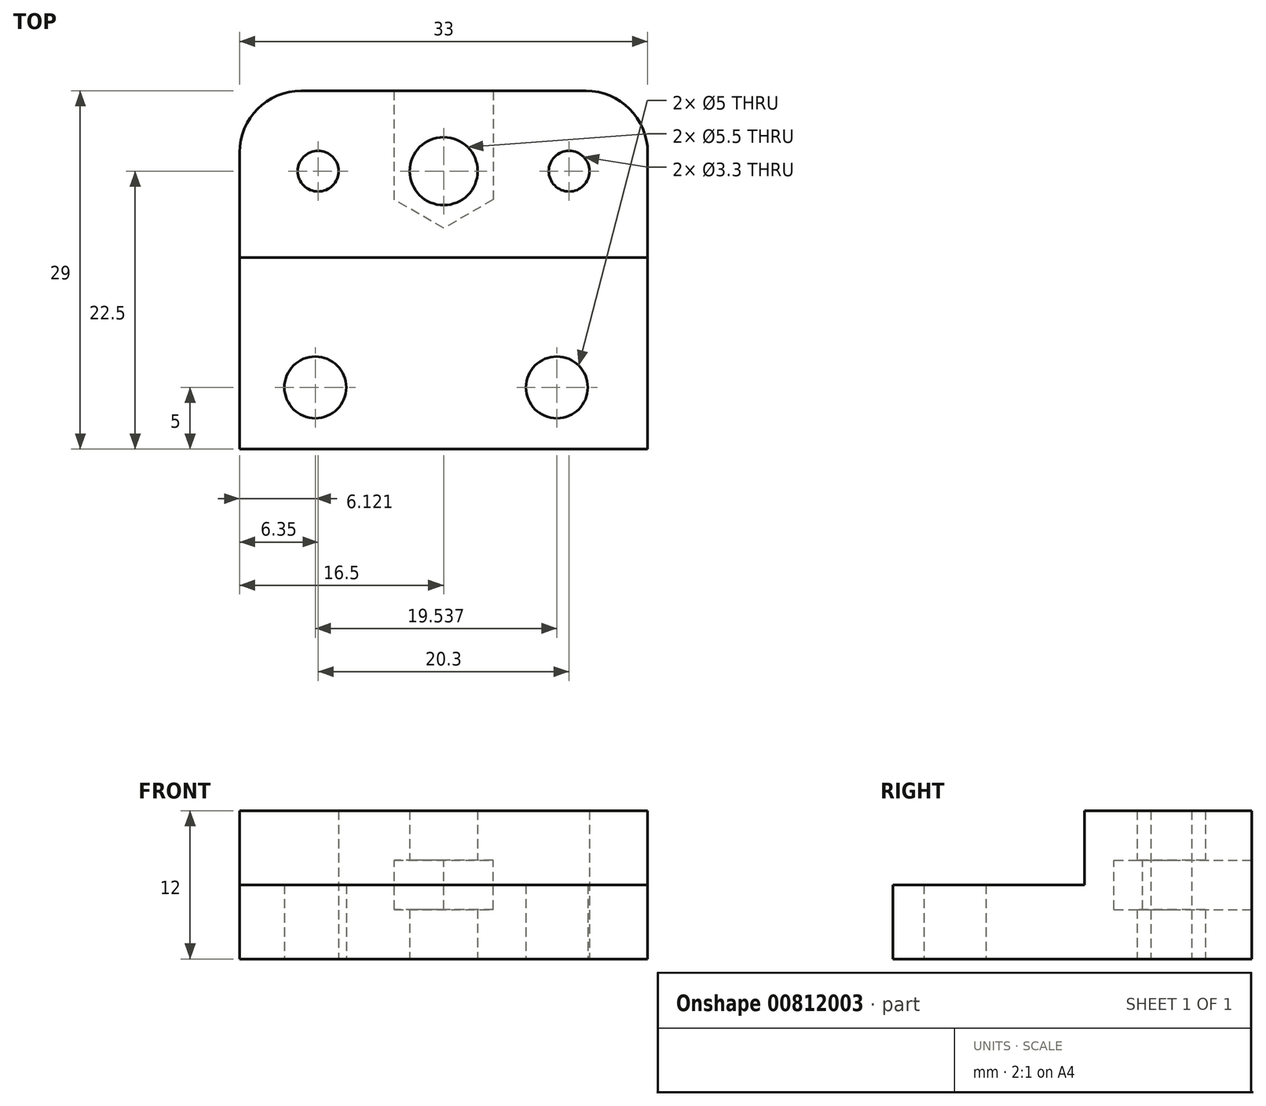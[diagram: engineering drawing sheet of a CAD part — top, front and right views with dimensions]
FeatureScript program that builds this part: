
annotation { "Feature Type Name" : "Feature", "Feature Type Description" : "" }
export const myFeature = defineFeature(function(context is Context, id is Id, definition is map)
    precondition{}
    {
        {
            var Q0;
            Q0=qCreatedBy(makeId("Top.planeOp"),FACE);
            var sketch = newSketch(context, id + "F0", { "sketchPlane" : qUnion([Q0])});
            skLineSegment(sketch, "E0.bottom", {"start": v(-16.5, 14.5) * mm, "end": v(16.5, 14.5) * mm});
            skLineSegment(sketch, "E0.top", {"start": v(-16.5, -14.5) * mm, "end": v(16.5, -14.5) * mm});
            skLineSegment(sketch, "E0.left", {"start": v(-16.5, 14.5) * mm, "end": v(-16.5, -14.5) * mm});
            skLineSegment(sketch, "E0.right", {"start": v(16.5, 14.5) * mm, "end": v(16.5, -14.5) * mm});
            skPoint(sketch, "E0.middle", {"position": v(0, 0) * mm});
            skCircle(sketch, "E1", {"center": v(0, 8) * mm, "radius": 2.75 * mm});
            skCircle(sketch, "E2", {"center": v(-10.38, -9.5) * mm, "radius": 2.5 * mm});
            skCircle(sketch, "E3", {"center": v(9.16, -9.5) * mm, "radius": 2.5 * mm});
            skLineSegment(sketch, "E4", {"start": v(-10.38, -9.5) * mm, "end": v(9.16, -9.5) * mm, "construction": true});
            skCircle(sketch, "E5", {"center": v(10.15, 8) * mm, "radius": 1.65 * mm});
            skCircle(sketch, "E6", {"center": v(-10.15, 8) * mm, "radius": 1.65 * mm});
            skCircle(sketch, "E7.cCircle", {"center": v(0, 8) * mm, "radius": 4 * mm, "construction": true});
            skLineSegment(sketch, "E7.0", {"start": v(4, 10.3) * mm, "end": v(4, 5.7) * mm});
            skLineSegment(sketch, "E7.1", {"start": v(4, 5.7) * mm, "end": v(0, 3.38) * mm});
            skLineSegment(sketch, "E7.2", {"start": v(0, 3.38) * mm, "end": v(-4, 5.7) * mm});
            skLineSegment(sketch, "E7.3", {"start": v(-4, 5.7) * mm, "end": v(-4, 10.12) * mm});
            skPoint(sketch, "E7.0.midPoint", {"position": v(4, 8) * mm});
            skPoint(sketch, "E8.orphan", {"position": v(0, 12.62) * mm});
            skLineSegment(sketch, "E9", {"start": v(-4, 10.12) * mm, "end": v(-4, 14.5) * mm});
            skLineSegment(sketch, "E10", {"start": v(4, 10.3) * mm, "end": v(4, 14.5) * mm});
            skLineSegment(sketch, "E11.top", {"start": v(-16.5, 1) * mm, "end": v(16.5, 1) * mm});
            skLineSegment(sketch, "E11.left", {"start": v(-16.5, -14.5) * mm, "end": v(-16.5, 1) * mm});
            skLineSegment(sketch, "E11.right", {"start": v(16.5, -14.5) * mm, "end": v(16.5, 1) * mm});
            skSolve(sketch);
        }
        {
            var Q0;
            Q0=makeQuery(id+"F0.imprint","IMPRINT",FACE,{"disambiguationData":[TD([[makeQuery(id+"F0.imprint","IMPRINT",EDGE,{"derivedFrom":sQuery(id+"F0.wireOp",EDGE,"E1")}),-1.0]])]});
            var Q1;
            Q1=makeQuery(id+"F0.imprint","IMPRINT",FACE,{"disambiguationData":[TD([[makeQuery(id+"F0.imprint","IMPRINT",EDGE,{"derivedFrom":sQuery(id+"F0.wireOp",EDGE,"E5")}),-1.0]])]});
            var Q2;
            {var subQ1=sQuery(id+"F0.wireOp",EDGE,"E0.top");Q2=makeQuery(id+"F0.imprint","IMPRINT",FACE,{"disambiguationData":[TD([[makeQuery(id+"F0.imprint","IMPRINT",EDGE,{"derivedFrom":subQ1}),1.0]])]});}
            extrude(context, id + "F1", {"entities" : qUnion([Q0, Q1, Q2]), "endBound" : BoundingType.SYMMETRIC, "depth" : 12 * mm, "offsetDistance" : 25 * mm});
        }
        {
            var Q0;
            Q0=makeQuery(id+"F1.opExtrude","SWEPT_EDGE",EDGE,{"disambiguationData":[OSD([sQuery(id+"F0.wireOp",EDGE,"E0.bottom"),sQuery(id+"F0.wireOp",EDGE,"E0.right")])]});
            var Q1;
            Q1=makeQuery(id+"F1.opExtrude","SWEPT_EDGE",EDGE,{"disambiguationData":[OSD([sQuery(id+"F0.wireOp",EDGE,"E0.bottom"),sQuery(id+"F0.wireOp",EDGE,"E0.left")])]});
            fillet(context, id + "F2", {"entities" : qUnion([Q0, Q1]), "radius" : 5 * mm, "tangentPropagation" : true, "allowEdgeOverflow" : false});
        }
        {
            var Q0;
            Q0=makeQuery(id+"F0.imprint","IMPRINT",FACE,{"disambiguationData":[TD([[makeQuery(id+"F0.imprint","IMPRINT",EDGE,{"derivedFrom":sQuery(id+"F0.wireOp",EDGE,"E1")}),-1.0]])]});
            extrude(context, id + "F3", {"entities" : qUnion([Q0]), "operationType" : NewBodyOperationType.REMOVE, "endBound" : BoundingType.SYMMETRIC, "oppositeDirection" : true, "depth" : 4 * mm, "offsetDistance" : 25 * mm});
        }
        {
            var Q0;
            {var subQ1=sQuery(id+"F0.wireOp",EDGE,"E0.top");Q0=makeQuery(id+"F0.imprint","IMPRINT",FACE,{"disambiguationData":[TD([[makeQuery(id+"F0.imprint","IMPRINT",EDGE,{"derivedFrom":subQ1}),1.0]])]});}
            extrude(context, id + "F4", {"entities" : qUnion([Q0]), "operationType" : NewBodyOperationType.REMOVE, "depth" : 25 * mm, "offsetDistance" : 25 * mm});
        }
    });
